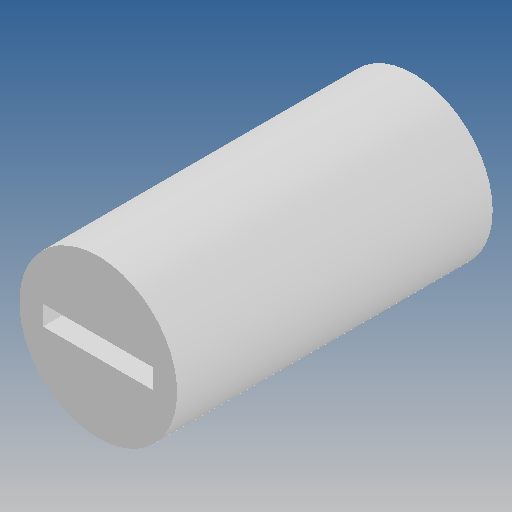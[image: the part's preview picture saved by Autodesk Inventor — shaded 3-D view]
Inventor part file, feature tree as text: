
AUTODESK INVENTOR PART (.ipt)
format: ipt  version: 2021 (Build 250183000, 183)  size: 124,928 bytes
history: native  units: in
note: dims shown in document units (in); Inventor stores cm internally (conversion verified against a paired STEP export)
features: extrude x3, sketch x3, other x3, reference x1
ambient origin geometry x8: Origin, YZ Plane, XZ Plane, XY Plane, X Axis, Y Axis, Z Axis, Center Point
bodies: Solid1 (feature_tree)
feature tree (10):
  extrude  "Extrusion1"  Depth=0.2441in
  extrude  "Extrusion2"  Depth=0.3937in TaperAngle=0.0deg
  extrude  "Extrusion3"  Depth=0.0984in
  sketch  "Sketch1"  dims[d0=0.7874in d1=0.2441in]
  reference  "Reference1"
  sketch  "Sketch2"  dims[d2=0.0079in d3=0.3937in d4=0.0in]
  sketch  "Sketch3"  dims[d5=0.5906in d6=0.0in d7=0.0984in d8=0.5512in d9=0.0492in d10=0.2756in d11=0.5906in d12=0.0in]
  other  "<userpath>\OneDrive\Objet3D\3DPrinter\3DPrinterBeltCoreXY.iam"
  other  "3DPrinterBeltCoreXY.iam"
  other  "DCMotor:1"
